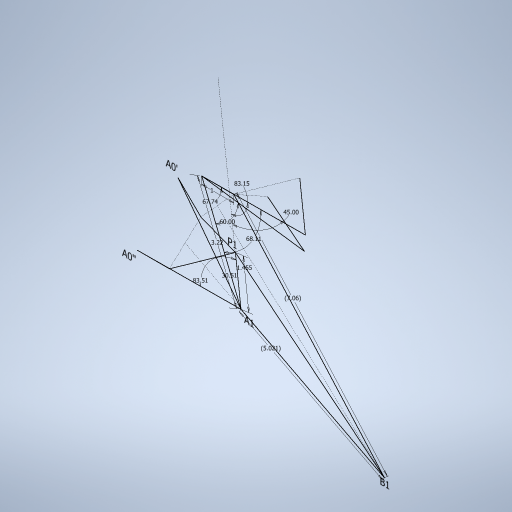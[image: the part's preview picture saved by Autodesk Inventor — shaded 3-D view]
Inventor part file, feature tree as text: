
AUTODESK INVENTOR PART (.ipt)
format: ipt  version: 2024 (Build 280153000, 153)  size: 260,608 bytes
history: native  units: in
note: dims shown in document units (in); Inventor stores cm internally (conversion verified against a paired STEP export)
features: sketch x1
ambient origin geometry x8: Origin, YZ Plane, XZ Plane, XY Plane, X Axis, Y Axis, Z Axis, Center Point
feature tree (1):
  sketch  "Sketch1"  dims[d0=0.1268in d1=0.0573in d2=0.0394in d7=0.4655in d10=0.6655in d11=60.0deg d13=135.0deg d14=0.468in d15=0.2096in d16=0.5738in d18=0.1977in d19=0.2779in]
